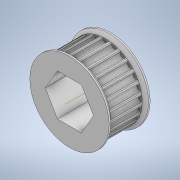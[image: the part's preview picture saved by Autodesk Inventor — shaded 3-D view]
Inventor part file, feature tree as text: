
AUTODESK INVENTOR PART (.ipt)
format: ipt  version: 2022.3 (Build 263350000, 350)  size: 333,824 bytes
history: native  units: in
note: dims shown in document units (in); Inventor stores cm internally (conversion verified against a paired STEP export)
features: extrude x7, sketch x7, fillet x2, pattern_circular x2, mirror x2, chamfer x2, other x1
ambient origin geometry x8: Origin, YZ Plane, XZ Plane, XY Plane, X Axis, Y Axis, Z Axis, Center Point
bodies: Solid1 (feature_tree)
feature tree (23):
  other  "Hex Bore"
  extrude  "HTD Base"  Depth=0.3937in TaperAngle=0.0deg
  extrude  "HTD Base Tooth"  Depth=0.0113in
  fillet  "HTD Base Tooth pt. 2"  [1 undecoded]
  pattern_circular  "HTD Teeth"  Count=24  [1 undecoded]
  extrude  "HTD Flange"  Depth=0.0394in
  mirror  "HTD Flanges"
  chamfer  "HTD Flange Chamfer"  Distance=0.0787in Angle=45.0deg
  extrude  "GT2 Base"  Depth=0.52in
  extrude  "GT2 Base Tooth"  TaperAngle=0.0deg  [1 undecoded]
  fillet  "GT2 Base Tooth pt. 2"  Radius=0.52in
  pattern_circular  "GT2 Teeth"  [2 undecoded]
  extrude  "GT2 Flange"  Depth=0.0591in
  mirror  "GT2 Flanges"
  chamfer  "GT2 Flange Chamfer"  Distance=0.3937in
  extrude  "Circle Bore"  TaperAngle=0.0deg  [1 undecoded]
  sketch  "Sketch1"  dims[d0=1.4588in d1=0.3937in d2=0.0in]
  sketch  "Sketch2"  dims[d3=0.1208in d5=0.0113in d6=0.0in d7=0.0in]
  sketch  "Sketch3"  dims[d8=0.0169in d9=9.4488in]
  sketch  "Sketch4"  dims[d10=360.0deg d12=0.0394in]
  sketch  "Sketch5"  dims[d13=0.0591in]
  sketch  "Sketch6"  dims[d14=0.0in]
  sketch  "Sketch7"  dims[d15=0.0394in d16=0.0787in d17=45.0deg d18=0.52in d19=0.0in d20=0.0in d21=0.52in d22=0.0in d23=0.0in d24=0.8723in d25=0.3937in d26=0.0in d27=0.0727in d28=0.0075in d29=0.0in d30=0.0in d31=0.0118in d32=9.4488in d33=360.0deg d35=0.0394in d36=0.0591in d37=0.0in d38=0.0394in d39=0.0787in d40=45.0deg]
note: 6 required parameter values undecoded (feature->parameter linkage not recoverable at this tier; creation-order binding heuristic only, values carry confidence <= 0.55)
